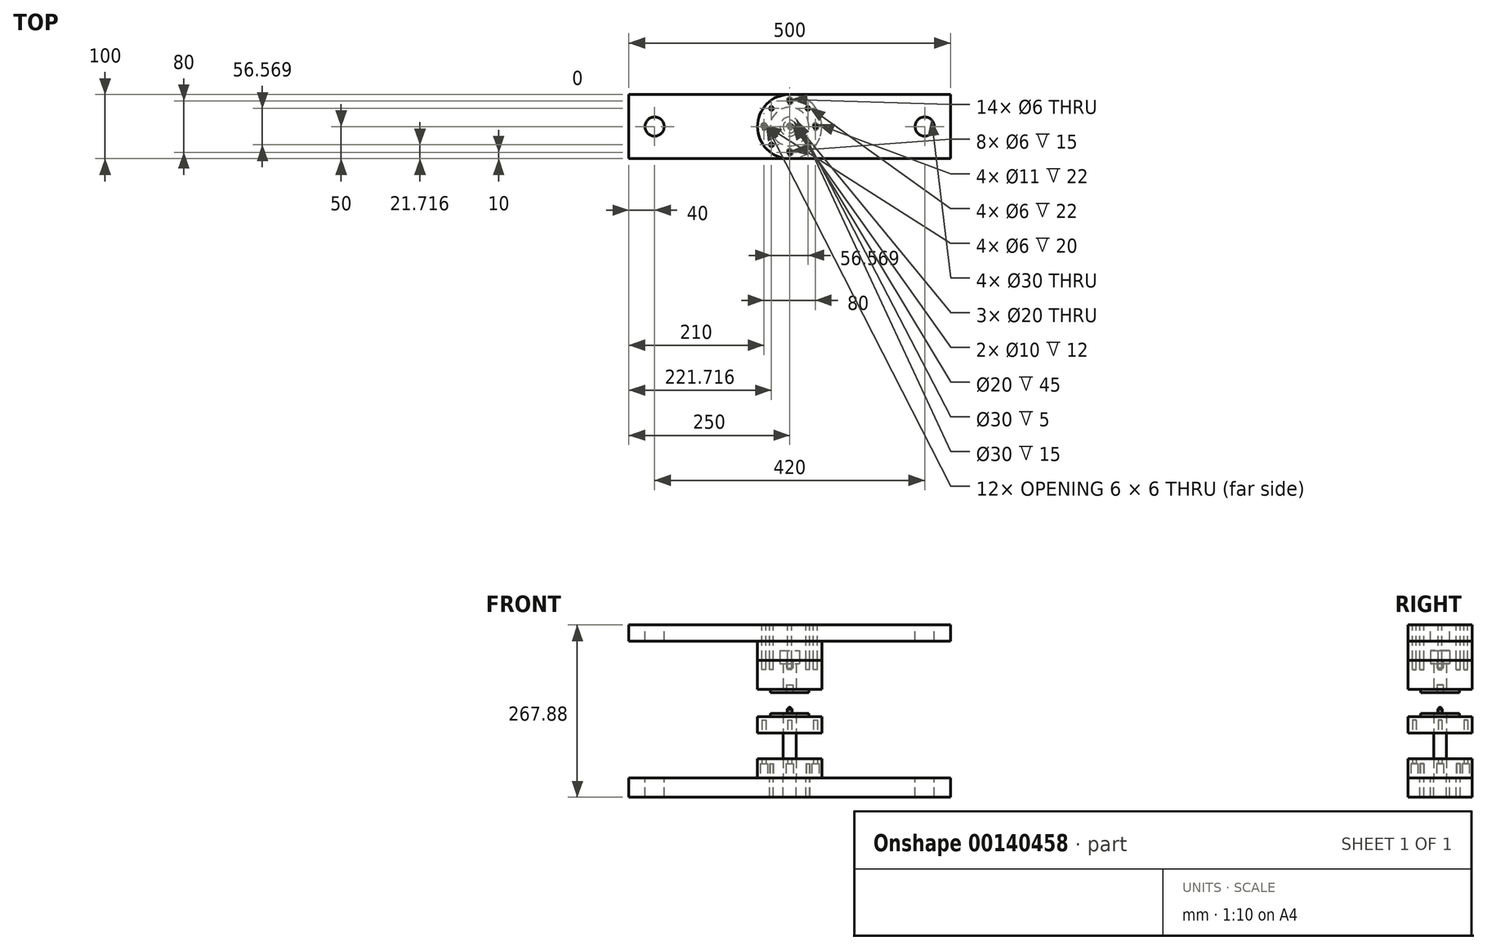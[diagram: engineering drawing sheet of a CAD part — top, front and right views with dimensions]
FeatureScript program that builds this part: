
annotation { "Feature Type Name" : "Feature", "Feature Type Description" : "" }
export const myFeature = defineFeature(function(context is Context, id is Id, definition is map)
    precondition{}
    {
        {
            var Q0;
            Q0=qCreatedBy(makeId("Front.planeOp"),FACE);
            var sketch = newSketch(context, id + "F0", { "sketchPlane" : qUnion([Q0])});
            skLineSegment(sketch, "E0", {"start": v(-30, 0) * mm, "end": v(-10, 0) * mm});
            skLineSegment(sketch, "E1", {"start": v(-30, 0) * mm, "end": v(-30, -5) * mm});
            skLineSegment(sketch, "E2", {"start": v(-50, -100) * mm, "end": v(0, -100) * mm});
            skLineSegment(sketch, "E3", {"start": v(0, -100) * mm, "end": v(0, 53.68) * mm, "construction": true});
            skPoint(sketch, "E3.endSnap0", {"position": v(0, -100) * mm});
            skLineSegment(sketch, "E4.0", {"start": v(-10, -100) * mm, "end": v(-10, 0) * mm});
            skLineSegment(sketch, "E5.0", {"start": v(-50, -30) * mm, "end": v(-10, -30) * mm});
            skLineSegment(sketch, "E6.0", {"start": v(-50, -70) * mm, "end": v(-10, -70) * mm});
            skLineSegment(sketch, "E7.0", {"start": v(-50, -100) * mm, "end": v(-50, -70) * mm});
            skLineSegment(sketch, "E8.0", {"start": v(-50, -5) * mm, "end": v(-30, -5) * mm});
            skLineSegment(sketch, "E9.0", {"start": v(-3.5, 0) * mm, "end": v(-3.5, 7) * mm});
            skLineSegment(sketch, "E10.0", {"start": v(-0.5, 10) * mm, "end": v(0, 10) * mm});
            skPoint(sketch, "E11.visualSharp", {"position": v(-3.5, 10) * mm});
            skArc(sketch, "E11.filletArc", {"start": v(-0.5, 10) * mm, "mid": v(-2.62, 9.12) * mm, "end": v(-3.5, 7) * mm});
            skPoint(sketch, "E12.visualSharp", {"position": v(3.5, 10) * mm});
            skLineSegment(sketch, "E13", {"start": v(-10, 0) * mm, "end": v(-3.5, 0) * mm});
            skLineSegment(sketch, "E14.trimOffspring", {"start": v(-50, -30) * mm, "end": v(-50, -5) * mm});
            skPoint(sketch, "E15.0.start.orphan", {"position": v(50, -100) * mm});
            skLineSegment(sketch, "E16", {"start": v(0, -100) * mm, "end": v(0, 10) * mm});
            skPoint(sketch, "E12.filletArc.end.orphan", {"position": v(0.5, 10) * mm});
            skSolve(sketch);
        }
        {
            var Q0;
            {var subQ2=sQuery(id+"F0.wireOp",EDGE,"E0");Q0=makeQuery(id+"F0.imprint","IMPRINT",FACE,{"disambiguationData":[TD([[makeQuery(id+"F0.imprint","IMPRINT",EDGE,{"derivedFrom":subQ2}),-1.0]])]});}
            var Q1;
            Q1=sQuery(id+"F0.wireOp",EDGE,"E3");
            revolve(context, id + "F1", {"entities" : qUnion([Q0]), "axis" : qUnion([Q1]), "revolveType" : RevolveType.FULL});
        }
        {
            var Q0;
            Q0=makeQuery(id+"F0.imprint","IMPRINT",FACE,{"disambiguationData":[TD([[makeQuery(id+"F0.imprint","IMPRINT",EDGE,{"derivedFrom":sQuery(id+"F0.wireOp",EDGE,"E9.0")}),-1.0]])]});
            var Q1;
            Q1=sQuery(id+"F0.wireOp",EDGE,"E3");
            revolve(context, id + "F2", {"entities" : qUnion([Q0]), "axis" : qUnion([Q1]), "revolveType" : RevolveType.FULL});
        }
        {
            var Q0;
            {var subQ4=sQuery(id+"F0.wireOp",EDGE,"E6.0");Q0=makeQuery(id+"F0.imprint","IMPRINT",FACE,{"disambiguationData":[TD([[makeQuery(id+"F0.imprint","IMPRINT",EDGE,{"derivedFrom":subQ4}),-1.0]])]});}
            var Q1;
            Q1=sQuery(id+"F0.wireOp",EDGE,"E3");
            revolve(context, id + "F3", {"entities" : qUnion([Q0]), "axis" : qUnion([Q1]), "revolveType" : RevolveType.FULL});
        }
        {
            var Q0;
            Q0=makeQuery(id+"F3.opRevolve","SWEPT_FACE",FACE,{"disambiguationData":[OSD([sQuery(id+"F0.wireOp",EDGE,"E2")])]});
            var sketch = newSketch(context, id + "F4", { "sketchPlane" : qUnion([Q0])});
            skCircle(sketch, "E17", {"center": v(-40, 0) * mm, "radius": 3 * mm});
            skCircle(sketch, "E18", {"center": v(0, 0) * mm, "radius": 40 * mm, "construction": true});
            skCircle(sketch, "E19.1.0", {"center": v(0, -40) * mm, "radius": 3 * mm});
            skCircle(sketch, "E19.2.0", {"center": v(40, 0) * mm, "radius": 3 * mm});
            skCircle(sketch, "E19.3.0", {"center": v(0, 40) * mm, "radius": 3 * mm});
            skCircle(sketch, "E20", {"center": v(-40, 0) * mm, "radius": 5.5 * mm});
            skCircle(sketch, "E21", {"center": v(0, -40) * mm, "radius": 5.5 * mm});
            skCircle(sketch, "E22", {"center": v(40, 0) * mm, "radius": 5.5 * mm});
            skCircle(sketch, "E23", {"center": v(0, 40) * mm, "radius": 5.5 * mm});
            skCircle(sketch, "E24.1.0", {"center": v(-28.28, 28.28) * mm, "radius": 3 * mm});
            skCircle(sketch, "E24.3.0", {"center": v(-28.28, -28.28) * mm, "radius": 3 * mm});
            skCircle(sketch, "E24.5.0", {"center": v(28.28, -28.28) * mm, "radius": 3 * mm});
            skCircle(sketch, "E24.7.0", {"center": v(28.28, 28.28) * mm, "radius": 3 * mm});
            skLineSegment(sketch, "E25.bottom", {"start": v(-250, -50) * mm, "end": v(250, -50) * mm});
            skLineSegment(sketch, "E25.top", {"start": v(-250, 50) * mm, "end": v(250, 50) * mm});
            skLineSegment(sketch, "E25.left", {"start": v(-250, -50) * mm, "end": v(-250, 50) * mm});
            skLineSegment(sketch, "E25.right", {"start": v(250, -50) * mm, "end": v(250, 50) * mm});
            skCircle(sketch, "E26", {"center": v(-28.28, 28.28) * mm, "radius": 3.15 * mm});
            skCircle(sketch, "E27", {"center": v(28.28, 28.28) * mm, "radius": 2.5 * mm});
            skCircle(sketch, "E28", {"center": v(-28.28, -28.28) * mm, "radius": 2.5 * mm});
            skCircle(sketch, "E29", {"center": v(28.28, -28.28) * mm, "radius": 3.15 * mm});
            skSolve(sketch);
        }
        {
            var Q0;
            Q0=makeQuery(id+"F4.imprint","IMPRINT",FACE,{"disambiguationData":[TD([[makeQuery(id+"F4.imprint","IMPRINT",EDGE,{"derivedFrom":sQuery(id+"F4.wireOp",EDGE,"E19.1.0")}),1.0]])]});
            var Q1;
            Q1=makeQuery(id+"F4.imprint","IMPRINT",FACE,{"disambiguationData":[TD([[makeQuery(id+"F4.imprint","IMPRINT",EDGE,{"derivedFrom":sQuery(id+"F4.wireOp",EDGE,"E17")}),1.0]])]});
            var Q2;
            Q2=makeQuery(id+"F4.imprint","IMPRINT",FACE,{"disambiguationData":[TD([[makeQuery(id+"F4.imprint","IMPRINT",EDGE,{"derivedFrom":sQuery(id+"F4.wireOp",EDGE,"E19.3.0")}),1.0]])]});
            var Q3;
            Q3=makeQuery(id+"F4.imprint","IMPRINT",FACE,{"disambiguationData":[TD([[makeQuery(id+"F4.imprint","IMPRINT",EDGE,{"derivedFrom":sQuery(id+"F4.wireOp",EDGE,"E19.2.0")}),1.0]])]});
            extrude(context, id + "F5", {"entities" : qUnion([Q0, Q1, Q2, Q3]), "operationType" : NewBodyOperationType.REMOVE, "oppositeDirection" : true, "depth" : 90 * mm});
        }
        {
            var Q0;
            Q0=makeQuery(id+"F4.imprint","IMPRINT",FACE,{"disambiguationData":[TD([[makeQuery(id+"F4.imprint","IMPRINT",EDGE,{"derivedFrom":sQuery(id+"F4.wireOp",EDGE,"E20")}),1.0]])]});
            var Q1;
            Q1=makeQuery(id+"F4.imprint","IMPRINT",FACE,{"disambiguationData":[TD([[makeQuery(id+"F4.imprint","IMPRINT",EDGE,{"derivedFrom":sQuery(id+"F4.wireOp",EDGE,"E21")}),1.0]])]});
            var Q2;
            Q2=makeQuery(id+"F4.imprint","IMPRINT",FACE,{"disambiguationData":[TD([[makeQuery(id+"F4.imprint","IMPRINT",EDGE,{"derivedFrom":sQuery(id+"F4.wireOp",EDGE,"E22")}),1.0]])]});
            var Q3;
            Q3=makeQuery(id+"F4.imprint","IMPRINT",FACE,{"disambiguationData":[TD([[makeQuery(id+"F4.imprint","IMPRINT",EDGE,{"derivedFrom":sQuery(id+"F4.wireOp",EDGE,"E19.3.0")}),-1.0]])]});
            var Q4;
            Q4=makeQuery(id+"F4.imprint","IMPRINT",FACE,{"disambiguationData":[TD([[makeQuery(id+"F4.imprint","IMPRINT",EDGE,{"derivedFrom":sQuery(id+"F4.wireOp",EDGE,"E24.5.0")}),1.0]])]});
            var Q5;
            Q5=makeQuery(id+"F4.imprint","IMPRINT",FACE,{"disambiguationData":[TD([[makeQuery(id+"F4.imprint","IMPRINT",EDGE,{"derivedFrom":sQuery(id+"F4.wireOp",EDGE,"E24.3.0")}),1.0]])]});
            var Q6;
            Q6=makeQuery(id+"F4.imprint","IMPRINT",FACE,{"disambiguationData":[TD([[makeQuery(id+"F4.imprint","IMPRINT",EDGE,{"derivedFrom":sQuery(id+"F4.wireOp",EDGE,"E24.1.0")}),1.0]])]});
            var Q7;
            Q7=makeQuery(id+"F4.imprint","IMPRINT",FACE,{"disambiguationData":[TD([[makeQuery(id+"F4.imprint","IMPRINT",EDGE,{"derivedFrom":sQuery(id+"F4.wireOp",EDGE,"E24.7.0")}),1.0]])]});
            extrude(context, id + "F6", {"entities" : qUnion([Q0, Q1, Q2, Q3, Q4, Q5, Q6, Q7]), "operationType" : NewBodyOperationType.REMOVE, "oppositeDirection" : true, "depth" : 22 * mm});
        }
        {
            var Q0;
            Q0=makeQuery(id+"F4.imprint","IMPRINT",FACE,{"disambiguationData":[TD([[makeQuery(id+"F4.imprint","IMPRINT",EDGE,{"derivedFrom":sQuery(id+"F4.wireOp",EDGE,"E25.bottom")}),1.0]])]});
            var Q1;
            Q1=makeQuery(id+"F4.imprint","IMPRINT",FACE,{"disambiguationData":[TD([[makeQuery(id+"F4.imprint","IMPRINT",EDGE,{"derivedFrom":sQuery(id+"F4.wireOp",EDGE,"E20")}),-1.0]])]});
            var Q2;
            Q2=makeQuery(id+"F4.imprint","IMPRINT",FACE,{"disambiguationData":[TD([[makeQuery(id+"F4.imprint","IMPRINT",EDGE,{"derivedFrom":sQuery(id+"F4.wireOp",EDGE,"E21")}),1.0]])]});
            var Q3;
            Q3=makeQuery(id+"F4.imprint","IMPRINT",FACE,{"disambiguationData":[TD([[makeQuery(id+"F4.imprint","IMPRINT",EDGE,{"derivedFrom":sQuery(id+"F4.wireOp",EDGE,"E19.1.0")}),1.0]])]});
            var Q4;
            Q4=makeQuery(id+"F4.imprint","IMPRINT",FACE,{"disambiguationData":[TD([[makeQuery(id+"F4.imprint","IMPRINT",EDGE,{"derivedFrom":sQuery(id+"F4.wireOp",EDGE,"E22")}),1.0]])]});
            var Q5;
            Q5=makeQuery(id+"F4.imprint","IMPRINT",FACE,{"disambiguationData":[TD([[makeQuery(id+"F4.imprint","IMPRINT",EDGE,{"derivedFrom":sQuery(id+"F4.wireOp",EDGE,"E19.2.0")}),1.0]])]});
            var Q6;
            Q6=makeQuery(id+"F4.imprint","IMPRINT",FACE,{"disambiguationData":[TD([[makeQuery(id+"F4.imprint","IMPRINT",EDGE,{"derivedFrom":sQuery(id+"F4.wireOp",EDGE,"E19.3.0")}),-1.0]])]});
            var Q7;
            Q7=makeQuery(id+"F4.imprint","IMPRINT",FACE,{"disambiguationData":[TD([[makeQuery(id+"F4.imprint","IMPRINT",EDGE,{"derivedFrom":sQuery(id+"F4.wireOp",EDGE,"E19.3.0")}),1.0]])]});
            var Q8;
            Q8=makeQuery(id+"F4.imprint","IMPRINT",FACE,{"disambiguationData":[TD([[makeQuery(id+"F4.imprint","IMPRINT",EDGE,{"derivedFrom":sQuery(id+"F4.wireOp",EDGE,"E20")}),1.0]])]});
            var Q9;
            Q9=makeQuery(id+"F4.imprint","IMPRINT",FACE,{"disambiguationData":[TD([[makeQuery(id+"F4.imprint","IMPRINT",EDGE,{"derivedFrom":sQuery(id+"F4.wireOp",EDGE,"E17")}),1.0]])]});
            extrude(context, id + "F7", {"entities" : qUnion([Q0, Q1, Q2, Q3, Q4, Q5, Q6, Q7, Q8, Q9]), "depth" : 30 * mm});
        }
        {
            var Q0;
            Q0=qCreatedBy(makeId("Front.planeOp"),FACE);
            var sketch = newSketch(context, id + "F8", { "sketchPlane" : qUnion([Q0])});
            skLineSegment(sketch, "E30.0", {"start": v(0, -100) * mm, "end": v(0, 70.88) * mm});
            skLineSegment(sketch, "E31", {"start": v(-5, 32.88) * mm, "end": v(-30, 32.88) * mm});
            skPoint(sketch, "E31.endSnap0", {"position": v(0, 32.88) * mm});
            skLineSegment(sketch, "E32.0", {"start": v(-50, 37.88) * mm, "end": v(-50, 82.88) * mm});
            skLineSegment(sketch, "E33.0", {"start": v(-30, 32.88) * mm, "end": v(-30, 37.88) * mm});
            skLineSegment(sketch, "E34.0", {"start": v(-5, 82.88) * mm, "end": v(-50, 82.88) * mm});
            skLineSegment(sketch, "E35.trimOffspring", {"start": v(-30, 37.88) * mm, "end": v(-50, 37.88) * mm});
            skLineSegment(sketch, "E36.0", {"start": v(-10, 32.88) * mm, "end": v(-10, 77.88) * mm});
            skLineSegment(sketch, "E37.0", {"start": v(-10, 77.88) * mm, "end": v(-15, 77.88) * mm});
            skLineSegment(sketch, "E38.0", {"start": v(-15, 77.88) * mm, "end": v(-15, 82.88) * mm});
            skLineSegment(sketch, "E39.0", {"start": v(0, 112.88) * mm, "end": v(-50, 112.88) * mm});
            skLineSegment(sketch, "E40", {"start": v(-15, 82.88) * mm, "end": v(-15, 97.88) * mm});
            skLineSegment(sketch, "E41", {"start": v(-50, 82.88) * mm, "end": v(-50, 112.88) * mm});
            skLineSegment(sketch, "E42.0", {"start": v(0, 97.88) * mm, "end": v(-15, 97.88) * mm});
            skLineSegment(sketch, "E43.0", {"start": v(-5, 32.88) * mm, "end": v(-5, 44.88) * mm});
            skLineSegment(sketch, "E44.0", {"start": v(0, 44.88) * mm, "end": v(-5, 44.88) * mm});
            skLineSegment(sketch, "E45.0", {"start": v(-5, -100) * mm, "end": v(-5, 82.88) * mm});
            skLineSegment(sketch, "E46.0", {"start": v(0, 70.88) * mm, "end": v(-5, 70.88) * mm});
            skLineSegment(sketch, "E47.trimOffspring", {"start": v(0, 97.88) * mm, "end": v(0, 112.88) * mm});
            skSolve(sketch);
        }
        {
            var Q0;
            {var subQ3=sQuery(id+"F8.wireOp",EDGE,"E36.0");Q0=makeQuery(id+"F8.imprint","IMPRINT",FACE,{"disambiguationData":[TD([[makeQuery(id+"F8.imprint","IMPRINT",EDGE,{"derivedFrom":subQ3}),-1.0]])]});}
            var Q1;
            {var subQ2=sQuery(id+"F8.wireOp",EDGE,"E44.0");Q1=makeQuery(id+"F8.imprint","IMPRINT",FACE,{"disambiguationData":[TD([[makeQuery(id+"F8.imprint","IMPRINT",EDGE,{"derivedFrom":subQ2}),-1.0]])]});}
            var Q2;
            Q2=sQuery(id+"F8.wireOp",EDGE,"E30.0");
            revolve(context, id + "F9", {"entities" : qUnion([Q0, Q1]), "axis" : qUnion([Q2]), "revolveType" : RevolveType.FULL});
        }
        {
            var Q0;
            {var subQ1=sQuery(id+"F8.wireOp",EDGE,"E32.0");Q0=makeQuery(id+"F8.imprint","IMPRINT",FACE,{"disambiguationData":[TD([[makeQuery(id+"F8.imprint","IMPRINT",EDGE,{"derivedFrom":subQ1}),-1.0]])]});}
            var Q1;
            Q1=sQuery(id+"F8.wireOp",EDGE,"E30.0");
            revolve(context, id + "F10", {"entities" : qUnion([Q0]), "axis" : qUnion([Q1]), "revolveType" : RevolveType.FULL});
        }
        {
            var Q0;
            Q0=makeQuery(id+"F8.imprint","IMPRINT",FACE,{"disambiguationData":[TD([[makeQuery(id+"F8.imprint","IMPRINT",EDGE,{"derivedFrom":sQuery(id+"F8.wireOp",EDGE,"E39.0")}),1.0]])]});
            var Q1;
            Q1=sQuery(id+"F8.wireOp",EDGE,"E47.trimOffspring");
            revolve(context, id + "F11", {"entities" : qUnion([Q0]), "axis" : qUnion([Q1]), "revolveType" : RevolveType.FULL});
        }
        {
            var Q0;
            Q0=makeQuery(id+"F11.opRevolve","SWEPT_FACE",FACE,{"disambiguationData":[OSD([sQuery(id+"F8.wireOp",EDGE,"E39.0")])]});
            var sketch = newSketch(context, id + "F12", { "sketchPlane" : qUnion([Q0])});
            skCircle(sketch, "E48", {"center": v(0, 0) * mm, "radius": 40 * mm, "construction": true});
            skCircle(sketch, "E49", {"center": v(-40, 0) * mm, "radius": 3 * mm});
            skCircle(sketch, "E50.1.0", {"center": v(-28.28, -28.28) * mm, "radius": 3 * mm});
            skCircle(sketch, "E50.2.0", {"center": v(0, -40) * mm, "radius": 3 * mm});
            skCircle(sketch, "E50.3.0", {"center": v(28.28, -28.28) * mm, "radius": 3 * mm});
            skCircle(sketch, "E50.4.0", {"center": v(40, 0) * mm, "radius": 3 * mm});
            skCircle(sketch, "E50.5.0", {"center": v(28.28, 28.28) * mm, "radius": 3 * mm});
            skCircle(sketch, "E50.6.0", {"center": v(0, 40) * mm, "radius": 3 * mm});
            skCircle(sketch, "E50.7.0", {"center": v(-28.28, 28.28) * mm, "radius": 3 * mm});
            skLineSegment(sketch, "E51.bottom", {"start": v(250, 50) * mm, "end": v(-250, 50) * mm});
            skLineSegment(sketch, "E51.top", {"start": v(250, -50) * mm, "end": v(-250, -50) * mm});
            skLineSegment(sketch, "E51.left", {"start": v(250, 50) * mm, "end": v(250, -50) * mm});
            skLineSegment(sketch, "E51.right", {"start": v(-250, 50) * mm, "end": v(-250, -50) * mm});
            skSolve(sketch);
        }
        {
            var Q0;
            Q0=makeQuery(id+"F12.imprint","IMPRINT",FACE,{"disambiguationData":[TD([[makeQuery(id+"F12.imprint","IMPRINT",EDGE,{"derivedFrom":sQuery(id+"F12.wireOp",EDGE,"E50.1.0")}),1.0]])]});
            var Q1;
            Q1=makeQuery(id+"F12.imprint","IMPRINT",FACE,{"disambiguationData":[TD([[makeQuery(id+"F12.imprint","IMPRINT",EDGE,{"derivedFrom":sQuery(id+"F12.wireOp",EDGE,"E50.3.0")}),1.0]])]});
            var Q2;
            Q2=makeQuery(id+"F12.imprint","IMPRINT",FACE,{"disambiguationData":[TD([[makeQuery(id+"F12.imprint","IMPRINT",EDGE,{"derivedFrom":sQuery(id+"F12.wireOp",EDGE,"E50.5.0")}),1.0]])]});
            var Q3;
            Q3=makeQuery(id+"F12.imprint","IMPRINT",FACE,{"disambiguationData":[TD([[makeQuery(id+"F12.imprint","IMPRINT",EDGE,{"derivedFrom":sQuery(id+"F12.wireOp",EDGE,"E50.7.0")}),1.0]])]});
            var Q4;
            Q4=makeQuery(id+"F12.imprint","IMPRINT",FACE,{"disambiguationData":[TD([[makeQuery(id+"F12.imprint","IMPRINT",EDGE,{"derivedFrom":sQuery(id+"F12.wireOp",EDGE,"E49")}),1.0]])]});
            var Q5;
            Q5=makeQuery(id+"F12.imprint","IMPRINT",FACE,{"disambiguationData":[TD([[makeQuery(id+"F12.imprint","IMPRINT",EDGE,{"derivedFrom":sQuery(id+"F12.wireOp",EDGE,"E50.2.0")}),1.0]])]});
            var Q6;
            Q6=makeQuery(id+"F12.imprint","IMPRINT",FACE,{"disambiguationData":[TD([[makeQuery(id+"F12.imprint","IMPRINT",EDGE,{"derivedFrom":sQuery(id+"F12.wireOp",EDGE,"E50.4.0")}),1.0]])]});
            var Q7;
            Q7=makeQuery(id+"F12.imprint","IMPRINT",FACE,{"disambiguationData":[TD([[makeQuery(id+"F12.imprint","IMPRINT",EDGE,{"derivedFrom":sQuery(id+"F12.wireOp",EDGE,"E50.6.0")}),1.0]])]});
            extrude(context, id + "F13", {"entities" : qUnion([Q0, Q1, Q2, Q3, Q4, Q5, Q6, Q7]), "operationType" : NewBodyOperationType.REMOVE, "oppositeDirection" : true, "depth" : 45 * mm});
        }
        {
            var Q0;
            {var subQ0=sQuery(id+"F12.wireOp",EDGE,"E51.right");Q0=makeQuery(id+"F12.imprint","IMPRINT",FACE,{"disambiguationData":[TD([[makeQuery(id+"F12.imprint","IMPRINT",EDGE,{"derivedFrom":subQ0}),1.0]])]});}
            var Q1;
            {var subQ0=sQuery(id+"F12.wireOp",EDGE,"E51.left");Q1=makeQuery(id+"F12.imprint","IMPRINT",FACE,{"disambiguationData":[TD([[makeQuery(id+"F12.imprint","IMPRINT",EDGE,{"derivedFrom":subQ0}),-1.0]])]});}
            var Q2;
            Q2=makeQuery(id+"F12.imprint","IMPRINT",FACE,{"disambiguationData":[TD([[makeQuery(id+"F12.imprint","IMPRINT",EDGE,{"derivedFrom":sQuery(id+"F12.wireOp",EDGE,"E49")}),-1.0]])]});
            extrude(context, id + "F14", {"entities" : qUnion([Q0, Q1, Q2]), "operationType" : NewBodyOperationType.ADD, "depth" : 25 * mm});
        }
        {
            var Q0;
            Q0=makeQuery(id+"F14.opExtrude","CAP_FACE",FACE,{"disambiguationData":[OSD([sQuery(id+"F12.wireOp",EDGE,"E49"),sQuery(id+"F12.wireOp",EDGE,"E50.1.0"),sQuery(id+"F12.wireOp",EDGE,"E50.2.0"),sQuery(id+"F12.wireOp",EDGE,"E50.3.0"),sQuery(id+"F12.wireOp",EDGE,"E50.4.0"),sQuery(id+"F12.wireOp",EDGE,"E50.5.0"),sQuery(id+"F12.wireOp",EDGE,"E50.6.0"),sQuery(id+"F12.wireOp",EDGE,"E50.7.0"),sQuery(id+"F12.wireOp",EDGE,"E51.bottom"),sQuery(id+"F12.wireOp",EDGE,"E51.top"),sQuery(id+"F12.wireOp",EDGE,"E51.left"),sQuery(id+"F12.wireOp",EDGE,"E51.right")])],"isStart":false});
            var sketch = newSketch(context, id + "F15", { "sketchPlane" : qUnion([Q0])});
            skCircle(sketch, "E52", {"center": v(-210, 0) * mm, "radius": 15 * mm});
            skCircle(sketch, "E53", {"center": v(210, 0) * mm, "radius": 15 * mm});
            skSolve(sketch);
        }
        {
            var Q0;
            Q0=makeQuery(id+"F15.imprint","IMPRINT",FACE,{"disambiguationData":[TD([[makeQuery(id+"F15.imprint","IMPRINT",EDGE,{"derivedFrom":sQuery(id+"F15.wireOp",EDGE,"E53")}),1.0]])]});
            var Q1;
            Q1=makeQuery(id+"F15.imprint","IMPRINT",FACE,{"disambiguationData":[TD([[makeQuery(id+"F15.imprint","IMPRINT",EDGE,{"derivedFrom":sQuery(id+"F15.wireOp",EDGE,"E52")}),1.0]])]});
            extrude(context, id + "F16", {"entities" : qUnion([Q0, Q1]), "operationType" : NewBodyOperationType.REMOVE, "oppositeDirection" : true, "depth" : 300 * mm});
        }
    });
